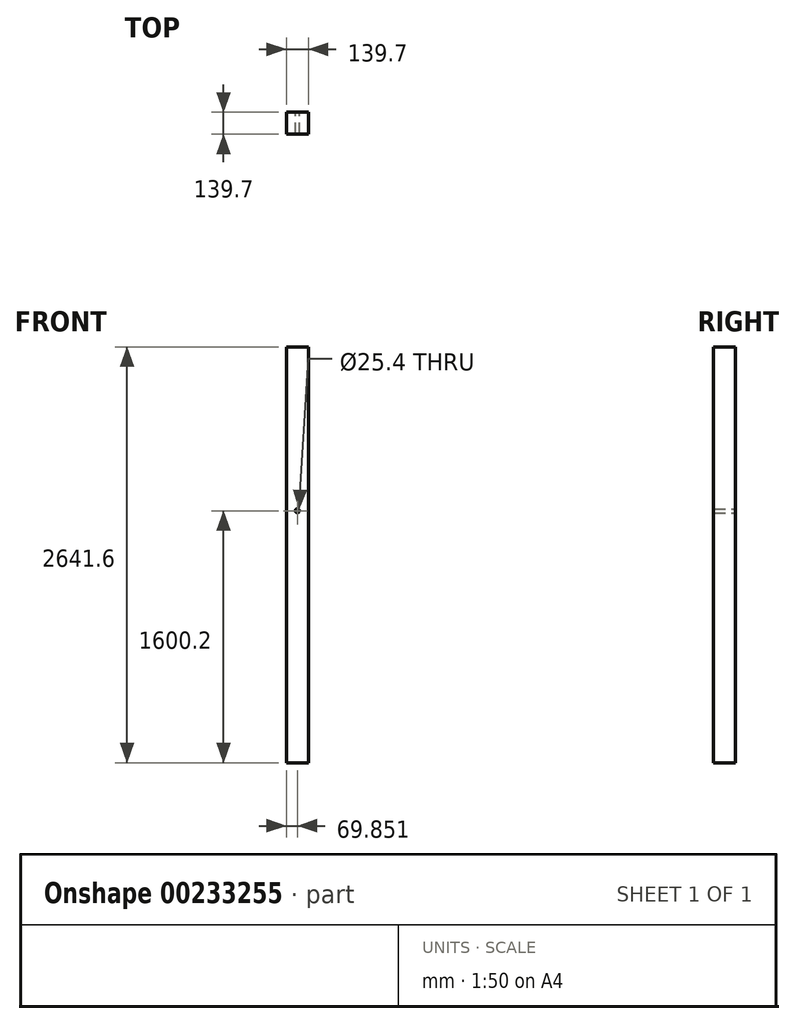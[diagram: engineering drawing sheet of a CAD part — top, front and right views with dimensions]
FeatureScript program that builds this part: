
annotation { "Feature Type Name" : "Feature", "Feature Type Description" : "" }
export const myFeature = defineFeature(function(context is Context, id is Id, definition is map)
    precondition{}
    {
        {
            var Q0;
            Q0=qCreatedBy(makeId("Front.planeOp"),FACE);
            var sketch = newSketch(context, id + "F0", { "sketchPlane" : qUnion([Q0])});
            skLineSegment(sketch, "E0.bottom", {"start": v(-80.82, 2570.88) * mm, "end": v(58.88, 2570.88) * mm});
            skLineSegment(sketch, "E0.top", {"start": v(-80.82, -70.72) * mm, "end": v(58.88, -70.72) * mm});
            skLineSegment(sketch, "E0.left", {"start": v(-80.82, 2570.88) * mm, "end": v(-80.82, -70.72) * mm});
            skLineSegment(sketch, "E0.right", {"start": v(58.88, 2570.88) * mm, "end": v(58.88, -70.72) * mm});
            skCircle(sketch, "E1", {"center": v(-10.97, 1529.48) * mm, "radius": 12.7 * mm});
            skSolve(sketch);
        }
        {
            var Q0;
            Q0=makeQuery(id+"F0.imprint","IMPRINT",FACE,{"disambiguationData":[TD([[makeQuery(id+"F0.imprint","IMPRINT",EDGE,{"derivedFrom":sQuery(id+"F0.wireOp",EDGE,"E0.bottom")}),-1.0]])]});
            extrude(context, id + "F1", {"entities" : qUnion([Q0]), "depth" : 139.7 * mm});
        }
    });
